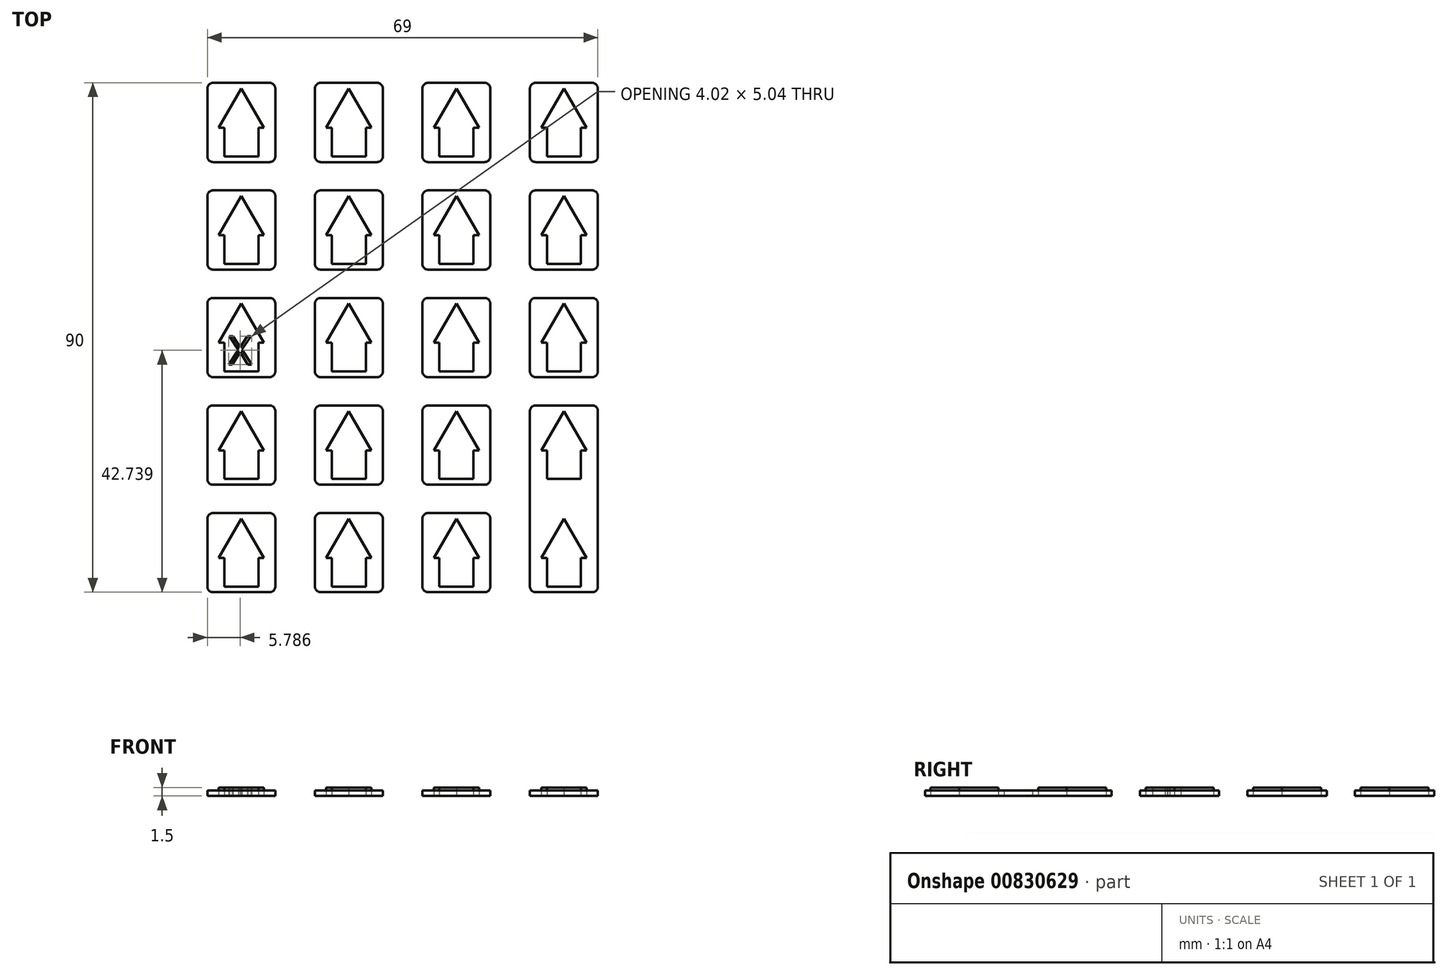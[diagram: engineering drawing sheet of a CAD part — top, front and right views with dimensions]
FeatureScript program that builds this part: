
annotation { "Feature Type Name" : "Feature", "Feature Type Description" : "" }
export const myFeature = defineFeature(function(context is Context, id is Id, definition is map)
    precondition{}
    {
        {
            var Q0;
            Q0=qCreatedBy(makeId("Top.planeOp"),FACE);
            var sketch = newSketch(context, id + "F0", { "sketchPlane" : qUnion([Q0])});
            skLineSegment(sketch, "E0.bottom", {"start": v(5, -7) * mm, "end": v(-5, -7) * mm});
            skLineSegment(sketch, "E0.top", {"start": v(5, 7) * mm, "end": v(-5, 7) * mm});
            skLineSegment(sketch, "E0.left", {"start": v(6, -6) * mm, "end": v(6, 6) * mm});
            skLineSegment(sketch, "E0.right", {"start": v(-6, -6) * mm, "end": v(-6, 6) * mm});
            skPoint(sketch, "E0.middle", {"position": v(0, 0) * mm});
            skPoint(sketch, "E1.visualSharp", {"position": v(-6, 7) * mm});
            skArc(sketch, "E1.filletArc", {"start": v(-5, 7) * mm, "mid": v(-5.7, 6.7) * mm, "end": v(-6, 6) * mm});
            skPoint(sketch, "E2.visualSharp", {"position": v(6, 7) * mm});
            skArc(sketch, "E2.filletArc", {"start": v(6, 6) * mm, "mid": v(5.7, 6.7) * mm, "end": v(5, 7) * mm});
            skPoint(sketch, "E3.visualSharp", {"position": v(6, -7) * mm});
            skArc(sketch, "E3.filletArc", {"start": v(5, -7) * mm, "mid": v(5.7, -6.7) * mm, "end": v(6, -6) * mm});
            skPoint(sketch, "E4.visualSharp", {"position": v(-6, -7) * mm});
            skArc(sketch, "E4.filletArc", {"start": v(-6, -6) * mm, "mid": v(-5.7, -6.7) * mm, "end": v(-5, -7) * mm});
            skLineSegment(sketch, "E5.0.1.0", {"start": v(6, 13) * mm, "end": v(6, 25) * mm});
            skLineSegment(sketch, "E5.0.1.1", {"start": v(-6, 13) * mm, "end": v(-6, 25) * mm});
            skLineSegment(sketch, "E5.0.1.2", {"start": v(5, 12) * mm, "end": v(-5, 12) * mm});
            skPoint(sketch, "E5.0.1.3", {"position": v(-6, 12) * mm});
            skPoint(sketch, "E5.0.1.4", {"position": v(0, 19) * mm});
            skPoint(sketch, "E5.0.1.5", {"position": v(-6, 26) * mm});
            skPoint(sketch, "E5.0.1.6", {"position": v(6, 26) * mm});
            skPoint(sketch, "E5.0.1.7", {"position": v(6, 12) * mm});
            skLineSegment(sketch, "E5.0.1.8", {"start": v(5, 26) * mm, "end": v(-5, 26) * mm});
            skArc(sketch, "E5.0.1.9", {"start": v(5, 12) * mm, "mid": v(5.7, 12.3) * mm, "end": v(6, 13) * mm});
            skArc(sketch, "E5.0.1.10", {"start": v(-6, 13) * mm, "mid": v(-5.7, 12.3) * mm, "end": v(-5, 12) * mm});
            skArc(sketch, "E5.0.1.11", {"start": v(6, 25) * mm, "mid": v(5.7, 25.7) * mm, "end": v(5, 26) * mm});
            skArc(sketch, "E5.0.1.12", {"start": v(-5, 26) * mm, "mid": v(-5.7, 25.7) * mm, "end": v(-6, 25) * mm});
            skLineSegment(sketch, "E5.0.2.0", {"start": v(6, 32) * mm, "end": v(6, 44) * mm});
            skLineSegment(sketch, "E5.0.2.1", {"start": v(-6, 32) * mm, "end": v(-6, 44) * mm});
            skLineSegment(sketch, "E5.0.2.2", {"start": v(5, 31) * mm, "end": v(-5, 31) * mm});
            skPoint(sketch, "E5.0.2.3", {"position": v(-6, 31) * mm});
            skPoint(sketch, "E5.0.2.4", {"position": v(0, 38) * mm});
            skPoint(sketch, "E5.0.2.5", {"position": v(-6, 45) * mm});
            skPoint(sketch, "E5.0.2.6", {"position": v(6, 45) * mm});
            skPoint(sketch, "E5.0.2.7", {"position": v(6, 31) * mm});
            skLineSegment(sketch, "E5.0.2.8", {"start": v(5, 45) * mm, "end": v(-5, 45) * mm});
            skArc(sketch, "E5.0.2.9", {"start": v(5, 31) * mm, "mid": v(5.7, 31.3) * mm, "end": v(6, 32) * mm});
            skArc(sketch, "E5.0.2.10", {"start": v(-6, 32) * mm, "mid": v(-5.7, 31.3) * mm, "end": v(-5, 31) * mm});
            skArc(sketch, "E5.0.2.11", {"start": v(6, 44) * mm, "mid": v(5.7, 44.7) * mm, "end": v(5, 45) * mm});
            skArc(sketch, "E5.0.2.12", {"start": v(-5, 45) * mm, "mid": v(-5.7, 44.7) * mm, "end": v(-6, 44) * mm});
            skLineSegment(sketch, "E5.0.3.0", {"start": v(6, 51) * mm, "end": v(6, 63) * mm});
            skLineSegment(sketch, "E5.0.3.1", {"start": v(-6, 51) * mm, "end": v(-6, 63) * mm});
            skLineSegment(sketch, "E5.0.3.2", {"start": v(5, 50) * mm, "end": v(-5, 50) * mm});
            skPoint(sketch, "E5.0.3.3", {"position": v(-6, 50) * mm});
            skPoint(sketch, "E5.0.3.4", {"position": v(0, 57) * mm});
            skPoint(sketch, "E5.0.3.5", {"position": v(-6, 64) * mm});
            skPoint(sketch, "E5.0.3.6", {"position": v(6, 64) * mm});
            skPoint(sketch, "E5.0.3.7", {"position": v(6, 50) * mm});
            skLineSegment(sketch, "E5.0.3.8", {"start": v(5, 64) * mm, "end": v(-5, 64) * mm});
            skArc(sketch, "E5.0.3.9", {"start": v(5, 50) * mm, "mid": v(5.7, 50.3) * mm, "end": v(6, 51) * mm});
            skArc(sketch, "E5.0.3.10", {"start": v(-6, 51) * mm, "mid": v(-5.7, 50.3) * mm, "end": v(-5, 50) * mm});
            skArc(sketch, "E5.0.3.11", {"start": v(6, 63) * mm, "mid": v(5.7, 63.7) * mm, "end": v(5, 64) * mm});
            skArc(sketch, "E5.0.3.12", {"start": v(-5, 64) * mm, "mid": v(-5.7, 63.7) * mm, "end": v(-6, 63) * mm});
            skLineSegment(sketch, "E5.0.4.0", {"start": v(6, 70) * mm, "end": v(6, 82) * mm});
            skLineSegment(sketch, "E5.0.4.1", {"start": v(-6, 70) * mm, "end": v(-6, 82) * mm});
            skLineSegment(sketch, "E5.0.4.2", {"start": v(5, 69) * mm, "end": v(-5, 69) * mm});
            skPoint(sketch, "E5.0.4.3", {"position": v(-6, 69) * mm});
            skPoint(sketch, "E5.0.4.4", {"position": v(0, 76) * mm});
            skPoint(sketch, "E5.0.4.5", {"position": v(-6, 83) * mm});
            skPoint(sketch, "E5.0.4.6", {"position": v(6, 83) * mm});
            skPoint(sketch, "E5.0.4.7", {"position": v(6, 69) * mm});
            skLineSegment(sketch, "E5.0.4.8", {"start": v(5, 83) * mm, "end": v(-5, 83) * mm});
            skArc(sketch, "E5.0.4.9", {"start": v(5, 69) * mm, "mid": v(5.7, 69.3) * mm, "end": v(6, 70) * mm});
            skArc(sketch, "E5.0.4.10", {"start": v(-6, 70) * mm, "mid": v(-5.7, 69.3) * mm, "end": v(-5, 69) * mm});
            skArc(sketch, "E5.0.4.11", {"start": v(6, 82) * mm, "mid": v(5.7, 82.7) * mm, "end": v(5, 83) * mm});
            skArc(sketch, "E5.0.4.12", {"start": v(-5, 83) * mm, "mid": v(-5.7, 82.7) * mm, "end": v(-6, 82) * mm});
            skLineSegment(sketch, "E5.1.0.0", {"start": v(25, -6) * mm, "end": v(25, 6) * mm});
            skLineSegment(sketch, "E5.1.0.1", {"start": v(13, -6) * mm, "end": v(13, 6) * mm});
            skLineSegment(sketch, "E5.1.0.2", {"start": v(24, -7) * mm, "end": v(14, -7) * mm});
            skPoint(sketch, "E5.1.0.3", {"position": v(13, -7) * mm});
            skPoint(sketch, "E5.1.0.4", {"position": v(19, 0) * mm});
            skPoint(sketch, "E5.1.0.5", {"position": v(13, 7) * mm});
            skPoint(sketch, "E5.1.0.6", {"position": v(25, 7) * mm});
            skPoint(sketch, "E5.1.0.7", {"position": v(25, -7) * mm});
            skLineSegment(sketch, "E5.1.0.8", {"start": v(24, 7) * mm, "end": v(14, 7) * mm});
            skArc(sketch, "E5.1.0.9", {"start": v(24, -7) * mm, "mid": v(24.7, -6.7) * mm, "end": v(25, -6) * mm});
            skArc(sketch, "E5.1.0.10", {"start": v(13, -6) * mm, "mid": v(13.3, -6.7) * mm, "end": v(14, -7) * mm});
            skArc(sketch, "E5.1.0.11", {"start": v(25, 6) * mm, "mid": v(24.7, 6.7) * mm, "end": v(24, 7) * mm});
            skArc(sketch, "E5.1.0.12", {"start": v(14, 7) * mm, "mid": v(13.3, 6.7) * mm, "end": v(13, 6) * mm});
            skLineSegment(sketch, "E5.1.1.0", {"start": v(25, 13) * mm, "end": v(25, 25) * mm});
            skLineSegment(sketch, "E5.1.1.1", {"start": v(13, 13) * mm, "end": v(13, 25) * mm});
            skLineSegment(sketch, "E5.1.1.2", {"start": v(24, 12) * mm, "end": v(14, 12) * mm});
            skPoint(sketch, "E5.1.1.3", {"position": v(13, 12) * mm});
            skPoint(sketch, "E5.1.1.4", {"position": v(19, 19) * mm});
            skPoint(sketch, "E5.1.1.5", {"position": v(13, 26) * mm});
            skPoint(sketch, "E5.1.1.6", {"position": v(25, 26) * mm});
            skPoint(sketch, "E5.1.1.7", {"position": v(25, 12) * mm});
            skLineSegment(sketch, "E5.1.1.8", {"start": v(24, 26) * mm, "end": v(14, 26) * mm});
            skArc(sketch, "E5.1.1.9", {"start": v(24, 12) * mm, "mid": v(24.7, 12.3) * mm, "end": v(25, 13) * mm});
            skArc(sketch, "E5.1.1.10", {"start": v(13, 13) * mm, "mid": v(13.3, 12.3) * mm, "end": v(14, 12) * mm});
            skArc(sketch, "E5.1.1.11", {"start": v(25, 25) * mm, "mid": v(24.7, 25.7) * mm, "end": v(24, 26) * mm});
            skArc(sketch, "E5.1.1.12", {"start": v(14, 26) * mm, "mid": v(13.3, 25.7) * mm, "end": v(13, 25) * mm});
            skLineSegment(sketch, "E5.1.2.0", {"start": v(25, 32) * mm, "end": v(25, 44) * mm});
            skLineSegment(sketch, "E5.1.2.1", {"start": v(13, 32) * mm, "end": v(13, 44) * mm});
            skLineSegment(sketch, "E5.1.2.2", {"start": v(24, 31) * mm, "end": v(14, 31) * mm});
            skPoint(sketch, "E5.1.2.3", {"position": v(13, 31) * mm});
            skPoint(sketch, "E5.1.2.4", {"position": v(19, 38) * mm});
            skPoint(sketch, "E5.1.2.5", {"position": v(13, 45) * mm});
            skPoint(sketch, "E5.1.2.6", {"position": v(25, 45) * mm});
            skPoint(sketch, "E5.1.2.7", {"position": v(25, 31) * mm});
            skLineSegment(sketch, "E5.1.2.8", {"start": v(24, 45) * mm, "end": v(14, 45) * mm});
            skArc(sketch, "E5.1.2.9", {"start": v(24, 31) * mm, "mid": v(24.7, 31.3) * mm, "end": v(25, 32) * mm});
            skArc(sketch, "E5.1.2.10", {"start": v(13, 32) * mm, "mid": v(13.3, 31.3) * mm, "end": v(14, 31) * mm});
            skArc(sketch, "E5.1.2.11", {"start": v(25, 44) * mm, "mid": v(24.7, 44.7) * mm, "end": v(24, 45) * mm});
            skArc(sketch, "E5.1.2.12", {"start": v(14, 45) * mm, "mid": v(13.3, 44.7) * mm, "end": v(13, 44) * mm});
            skLineSegment(sketch, "E5.1.3.0", {"start": v(25, 51) * mm, "end": v(25, 63) * mm});
            skLineSegment(sketch, "E5.1.3.1", {"start": v(13, 51) * mm, "end": v(13, 63) * mm});
            skLineSegment(sketch, "E5.1.3.2", {"start": v(24, 50) * mm, "end": v(14, 50) * mm});
            skPoint(sketch, "E5.1.3.3", {"position": v(13, 50) * mm});
            skPoint(sketch, "E5.1.3.4", {"position": v(19, 57) * mm});
            skPoint(sketch, "E5.1.3.5", {"position": v(13, 64) * mm});
            skPoint(sketch, "E5.1.3.6", {"position": v(25, 64) * mm});
            skPoint(sketch, "E5.1.3.7", {"position": v(25, 50) * mm});
            skLineSegment(sketch, "E5.1.3.8", {"start": v(24, 64) * mm, "end": v(14, 64) * mm});
            skArc(sketch, "E5.1.3.9", {"start": v(24, 50) * mm, "mid": v(24.7, 50.3) * mm, "end": v(25, 51) * mm});
            skArc(sketch, "E5.1.3.10", {"start": v(13, 51) * mm, "mid": v(13.3, 50.3) * mm, "end": v(14, 50) * mm});
            skArc(sketch, "E5.1.3.11", {"start": v(25, 63) * mm, "mid": v(24.7, 63.7) * mm, "end": v(24, 64) * mm});
            skArc(sketch, "E5.1.3.12", {"start": v(14, 64) * mm, "mid": v(13.3, 63.7) * mm, "end": v(13, 63) * mm});
            skLineSegment(sketch, "E5.1.4.0", {"start": v(25, 70) * mm, "end": v(25, 82) * mm});
            skLineSegment(sketch, "E5.1.4.1", {"start": v(13, 70) * mm, "end": v(13, 82) * mm});
            skLineSegment(sketch, "E5.1.4.2", {"start": v(24, 69) * mm, "end": v(14, 69) * mm});
            skPoint(sketch, "E5.1.4.3", {"position": v(13, 69) * mm});
            skPoint(sketch, "E5.1.4.4", {"position": v(19, 76) * mm});
            skPoint(sketch, "E5.1.4.5", {"position": v(13, 83) * mm});
            skPoint(sketch, "E5.1.4.6", {"position": v(25, 83) * mm});
            skPoint(sketch, "E5.1.4.7", {"position": v(25, 69) * mm});
            skLineSegment(sketch, "E5.1.4.8", {"start": v(24, 83) * mm, "end": v(14, 83) * mm});
            skArc(sketch, "E5.1.4.9", {"start": v(24, 69) * mm, "mid": v(24.7, 69.3) * mm, "end": v(25, 70) * mm});
            skArc(sketch, "E5.1.4.10", {"start": v(13, 70) * mm, "mid": v(13.3, 69.3) * mm, "end": v(14, 69) * mm});
            skArc(sketch, "E5.1.4.11", {"start": v(25, 82) * mm, "mid": v(24.7, 82.7) * mm, "end": v(24, 83) * mm});
            skArc(sketch, "E5.1.4.12", {"start": v(14, 83) * mm, "mid": v(13.3, 82.7) * mm, "end": v(13, 82) * mm});
            skLineSegment(sketch, "E5.2.0.0", {"start": v(44, -6) * mm, "end": v(44, 6) * mm});
            skLineSegment(sketch, "E5.2.0.1", {"start": v(32, -6) * mm, "end": v(32, 6) * mm});
            skLineSegment(sketch, "E5.2.0.2", {"start": v(43, -7) * mm, "end": v(33, -7) * mm});
            skPoint(sketch, "E5.2.0.3", {"position": v(32, -7) * mm});
            skPoint(sketch, "E5.2.0.4", {"position": v(38, 0) * mm});
            skPoint(sketch, "E5.2.0.5", {"position": v(32, 7) * mm});
            skPoint(sketch, "E5.2.0.6", {"position": v(44, 7) * mm});
            skPoint(sketch, "E5.2.0.7", {"position": v(44, -7) * mm});
            skLineSegment(sketch, "E5.2.0.8", {"start": v(43, 7) * mm, "end": v(33, 7) * mm});
            skArc(sketch, "E5.2.0.9", {"start": v(43, -7) * mm, "mid": v(43.7, -6.7) * mm, "end": v(44, -6) * mm});
            skArc(sketch, "E5.2.0.10", {"start": v(32, -6) * mm, "mid": v(32.3, -6.7) * mm, "end": v(33, -7) * mm});
            skArc(sketch, "E5.2.0.11", {"start": v(44, 6) * mm, "mid": v(43.7, 6.7) * mm, "end": v(43, 7) * mm});
            skArc(sketch, "E5.2.0.12", {"start": v(33, 7) * mm, "mid": v(32.3, 6.7) * mm, "end": v(32, 6) * mm});
            skLineSegment(sketch, "E5.2.1.0", {"start": v(44, 13) * mm, "end": v(44, 25) * mm});
            skLineSegment(sketch, "E5.2.1.1", {"start": v(32, 13) * mm, "end": v(32, 25) * mm});
            skLineSegment(sketch, "E5.2.1.2", {"start": v(43, 12) * mm, "end": v(33, 12) * mm});
            skPoint(sketch, "E5.2.1.3", {"position": v(32, 12) * mm});
            skPoint(sketch, "E5.2.1.4", {"position": v(38, 19) * mm});
            skPoint(sketch, "E5.2.1.5", {"position": v(32, 26) * mm});
            skPoint(sketch, "E5.2.1.6", {"position": v(44, 26) * mm});
            skPoint(sketch, "E5.2.1.7", {"position": v(44, 12) * mm});
            skLineSegment(sketch, "E5.2.1.8", {"start": v(43, 26) * mm, "end": v(33, 26) * mm});
            skArc(sketch, "E5.2.1.9", {"start": v(43, 12) * mm, "mid": v(43.7, 12.3) * mm, "end": v(44, 13) * mm});
            skArc(sketch, "E5.2.1.10", {"start": v(32, 13) * mm, "mid": v(32.3, 12.3) * mm, "end": v(33, 12) * mm});
            skArc(sketch, "E5.2.1.11", {"start": v(44, 25) * mm, "mid": v(43.7, 25.7) * mm, "end": v(43, 26) * mm});
            skArc(sketch, "E5.2.1.12", {"start": v(33, 26) * mm, "mid": v(32.3, 25.7) * mm, "end": v(32, 25) * mm});
            skLineSegment(sketch, "E5.2.2.0", {"start": v(44, 32) * mm, "end": v(44, 44) * mm});
            skLineSegment(sketch, "E5.2.2.1", {"start": v(32, 32) * mm, "end": v(32, 44) * mm});
            skLineSegment(sketch, "E5.2.2.2", {"start": v(43, 31) * mm, "end": v(33, 31) * mm});
            skPoint(sketch, "E5.2.2.3", {"position": v(32, 31) * mm});
            skPoint(sketch, "E5.2.2.4", {"position": v(38, 38) * mm});
            skPoint(sketch, "E5.2.2.5", {"position": v(32, 45) * mm});
            skPoint(sketch, "E5.2.2.6", {"position": v(44, 45) * mm});
            skPoint(sketch, "E5.2.2.7", {"position": v(44, 31) * mm});
            skLineSegment(sketch, "E5.2.2.8", {"start": v(43, 45) * mm, "end": v(33, 45) * mm});
            skArc(sketch, "E5.2.2.9", {"start": v(43, 31) * mm, "mid": v(43.7, 31.3) * mm, "end": v(44, 32) * mm});
            skArc(sketch, "E5.2.2.10", {"start": v(32, 32) * mm, "mid": v(32.3, 31.3) * mm, "end": v(33, 31) * mm});
            skArc(sketch, "E5.2.2.11", {"start": v(44, 44) * mm, "mid": v(43.7, 44.7) * mm, "end": v(43, 45) * mm});
            skArc(sketch, "E5.2.2.12", {"start": v(33, 45) * mm, "mid": v(32.3, 44.7) * mm, "end": v(32, 44) * mm});
            skLineSegment(sketch, "E5.2.3.0", {"start": v(44, 51) * mm, "end": v(44, 63) * mm});
            skLineSegment(sketch, "E5.2.3.1", {"start": v(32, 51) * mm, "end": v(32, 63) * mm});
            skLineSegment(sketch, "E5.2.3.2", {"start": v(43, 50) * mm, "end": v(33, 50) * mm});
            skPoint(sketch, "E5.2.3.3", {"position": v(32, 50) * mm});
            skPoint(sketch, "E5.2.3.4", {"position": v(38, 57) * mm});
            skPoint(sketch, "E5.2.3.5", {"position": v(32, 64) * mm});
            skPoint(sketch, "E5.2.3.6", {"position": v(44, 64) * mm});
            skPoint(sketch, "E5.2.3.7", {"position": v(44, 50) * mm});
            skLineSegment(sketch, "E5.2.3.8", {"start": v(43, 64) * mm, "end": v(33, 64) * mm});
            skArc(sketch, "E5.2.3.9", {"start": v(43, 50) * mm, "mid": v(43.7, 50.3) * mm, "end": v(44, 51) * mm});
            skArc(sketch, "E5.2.3.10", {"start": v(32, 51) * mm, "mid": v(32.3, 50.3) * mm, "end": v(33, 50) * mm});
            skArc(sketch, "E5.2.3.11", {"start": v(44, 63) * mm, "mid": v(43.7, 63.7) * mm, "end": v(43, 64) * mm});
            skArc(sketch, "E5.2.3.12", {"start": v(33, 64) * mm, "mid": v(32.3, 63.7) * mm, "end": v(32, 63) * mm});
            skLineSegment(sketch, "E5.2.4.0", {"start": v(44, 70) * mm, "end": v(44, 82) * mm});
            skLineSegment(sketch, "E5.2.4.1", {"start": v(32, 70) * mm, "end": v(32, 82) * mm});
            skLineSegment(sketch, "E5.2.4.2", {"start": v(43, 69) * mm, "end": v(33, 69) * mm});
            skPoint(sketch, "E5.2.4.3", {"position": v(32, 69) * mm});
            skPoint(sketch, "E5.2.4.4", {"position": v(38, 76) * mm});
            skPoint(sketch, "E5.2.4.5", {"position": v(32, 83) * mm});
            skPoint(sketch, "E5.2.4.6", {"position": v(44, 83) * mm});
            skPoint(sketch, "E5.2.4.7", {"position": v(44, 69) * mm});
            skLineSegment(sketch, "E5.2.4.8", {"start": v(43, 83) * mm, "end": v(33, 83) * mm});
            skArc(sketch, "E5.2.4.9", {"start": v(43, 69) * mm, "mid": v(43.7, 69.3) * mm, "end": v(44, 70) * mm});
            skArc(sketch, "E5.2.4.10", {"start": v(32, 70) * mm, "mid": v(32.3, 69.3) * mm, "end": v(33, 69) * mm});
            skArc(sketch, "E5.2.4.11", {"start": v(44, 82) * mm, "mid": v(43.7, 82.7) * mm, "end": v(43, 83) * mm});
            skArc(sketch, "E5.2.4.12", {"start": v(33, 83) * mm, "mid": v(32.3, 82.7) * mm, "end": v(32, 82) * mm});
            skLineSegment(sketch, "E5.3.0.2", {"start": v(62, -7) * mm, "end": v(52, -7) * mm});
            skPoint(sketch, "E5.3.0.3", {"position": v(51, -7) * mm});
            skPoint(sketch, "E5.3.0.4", {"position": v(57, 0) * mm});
            skPoint(sketch, "E5.3.0.7", {"position": v(63, -7) * mm});
            skArc(sketch, "E5.3.0.9", {"start": v(62, -7) * mm, "mid": v(62.7, -6.7) * mm, "end": v(63, -6) * mm});
            skArc(sketch, "E5.3.0.10", {"start": v(51, -6) * mm, "mid": v(51.3, -6.7) * mm, "end": v(52, -7) * mm});
            skLineSegment(sketch, "E5.3.1.0", {"start": v(63, -6) * mm, "end": v(63, 25) * mm});
            skLineSegment(sketch, "E5.3.1.1", {"start": v(51, -6) * mm, "end": v(51, 25) * mm});
            skPoint(sketch, "E5.3.1.4", {"position": v(57, 19) * mm});
            skPoint(sketch, "E5.3.1.5", {"position": v(51, 26) * mm});
            skPoint(sketch, "E5.3.1.6", {"position": v(63, 26) * mm});
            skLineSegment(sketch, "E5.3.1.8", {"start": v(62, 26) * mm, "end": v(52, 26) * mm});
            skArc(sketch, "E5.3.1.11", {"start": v(63, 25) * mm, "mid": v(62.7, 25.7) * mm, "end": v(62, 26) * mm});
            skArc(sketch, "E5.3.1.12", {"start": v(52, 26) * mm, "mid": v(51.3, 25.7) * mm, "end": v(51, 25) * mm});
            skLineSegment(sketch, "E5.3.2.0", {"start": v(63, 32) * mm, "end": v(63, 44) * mm});
            skLineSegment(sketch, "E5.3.2.1", {"start": v(51, 32) * mm, "end": v(51, 44) * mm});
            skLineSegment(sketch, "E5.3.2.2", {"start": v(62, 31) * mm, "end": v(52, 31) * mm});
            skPoint(sketch, "E5.3.2.3", {"position": v(51, 31) * mm});
            skPoint(sketch, "E5.3.2.4", {"position": v(57, 38) * mm});
            skPoint(sketch, "E5.3.2.5", {"position": v(51, 45) * mm});
            skPoint(sketch, "E5.3.2.6", {"position": v(63, 45) * mm});
            skPoint(sketch, "E5.3.2.7", {"position": v(63, 31) * mm});
            skLineSegment(sketch, "E5.3.2.8", {"start": v(62, 45) * mm, "end": v(52, 45) * mm});
            skArc(sketch, "E5.3.2.9", {"start": v(62, 31) * mm, "mid": v(62.7, 31.3) * mm, "end": v(63, 32) * mm});
            skArc(sketch, "E5.3.2.10", {"start": v(51, 32) * mm, "mid": v(51.3, 31.3) * mm, "end": v(52, 31) * mm});
            skArc(sketch, "E5.3.2.11", {"start": v(63, 44) * mm, "mid": v(62.7, 44.7) * mm, "end": v(62, 45) * mm});
            skArc(sketch, "E5.3.2.12", {"start": v(52, 45) * mm, "mid": v(51.3, 44.7) * mm, "end": v(51, 44) * mm});
            skLineSegment(sketch, "E5.3.3.0", {"start": v(63, 51) * mm, "end": v(63, 63) * mm});
            skLineSegment(sketch, "E5.3.3.1", {"start": v(51, 51) * mm, "end": v(51, 63) * mm});
            skLineSegment(sketch, "E5.3.3.2", {"start": v(62, 50) * mm, "end": v(52, 50) * mm});
            skPoint(sketch, "E5.3.3.3", {"position": v(51, 50) * mm});
            skPoint(sketch, "E5.3.3.4", {"position": v(57, 57) * mm});
            skPoint(sketch, "E5.3.3.5", {"position": v(51, 64) * mm});
            skPoint(sketch, "E5.3.3.6", {"position": v(63, 64) * mm});
            skPoint(sketch, "E5.3.3.7", {"position": v(63, 50) * mm});
            skLineSegment(sketch, "E5.3.3.8", {"start": v(62, 64) * mm, "end": v(52, 64) * mm});
            skArc(sketch, "E5.3.3.9", {"start": v(62, 50) * mm, "mid": v(62.7, 50.3) * mm, "end": v(63, 51) * mm});
            skArc(sketch, "E5.3.3.10", {"start": v(51, 51) * mm, "mid": v(51.3, 50.3) * mm, "end": v(52, 50) * mm});
            skArc(sketch, "E5.3.3.11", {"start": v(63, 63) * mm, "mid": v(62.7, 63.7) * mm, "end": v(62, 64) * mm});
            skArc(sketch, "E5.3.3.12", {"start": v(52, 64) * mm, "mid": v(51.3, 63.7) * mm, "end": v(51, 63) * mm});
            skLineSegment(sketch, "E5.3.4.0", {"start": v(63, 70) * mm, "end": v(63, 82) * mm});
            skLineSegment(sketch, "E5.3.4.1", {"start": v(51, 70) * mm, "end": v(51, 82) * mm});
            skLineSegment(sketch, "E5.3.4.2", {"start": v(62, 69) * mm, "end": v(52, 69) * mm});
            skPoint(sketch, "E5.3.4.3", {"position": v(51, 69) * mm});
            skPoint(sketch, "E5.3.4.4", {"position": v(57, 76) * mm});
            skPoint(sketch, "E5.3.4.5", {"position": v(51, 83) * mm});
            skPoint(sketch, "E5.3.4.6", {"position": v(63, 83) * mm});
            skPoint(sketch, "E5.3.4.7", {"position": v(63, 69) * mm});
            skLineSegment(sketch, "E5.3.4.8", {"start": v(62, 83) * mm, "end": v(52, 83) * mm});
            skArc(sketch, "E5.3.4.9", {"start": v(62, 69) * mm, "mid": v(62.7, 69.3) * mm, "end": v(63, 70) * mm});
            skArc(sketch, "E5.3.4.10", {"start": v(51, 70) * mm, "mid": v(51.3, 69.3) * mm, "end": v(52, 69) * mm});
            skArc(sketch, "E5.3.4.11", {"start": v(63, 82) * mm, "mid": v(62.7, 82.7) * mm, "end": v(62, 83) * mm});
            skArc(sketch, "E5.3.4.12", {"start": v(52, 83) * mm, "mid": v(51.3, 82.7) * mm, "end": v(51, 82) * mm});
            skLineSegment(sketch, "E5.direction1", {"start": v(-6, -7) * mm, "end": v(13, -7) * mm, "construction": true});
            skLineSegment(sketch, "E5.direction2", {"start": v(-6, -7) * mm, "end": v(-6, 12) * mm, "construction": true});
            skSolve(sketch);
        }
        {
            var Q0;
            Q0 = qSketchRegion(id + "F0", true);
            extrude(context, id + "F1", {"entities" : qUnion([Q0]), "depth" : 1 * mm, "offsetDistance" : 25 * mm});
        }
        {
            var Q0;
            Q0=qCreatedBy(makeId("Top.planeOp"),FACE);
            var sketch = newSketch(context, id + "F2", { "sketchPlane" : qUnion([Q0])});
            skLineSegment(sketch, "E6.bottom", {"start": v(3, -0.93) * mm, "end": v(4, -0.93) * mm});
            skLineSegment(sketch, "E6.top", {"start": v(-3, -6) * mm, "end": v(3, -6) * mm});
            skLineSegment(sketch, "E6.left", {"start": v(-3, -0.93) * mm, "end": v(-3, -6) * mm});
            skLineSegment(sketch, "E6.right", {"start": v(3, -0.93) * mm, "end": v(3, -6) * mm});
            skLineSegment(sketch, "E7", {"start": v(-4, -0.93) * mm, "end": v(0, 6) * mm});
            skLineSegment(sketch, "E8", {"start": v(0, 6) * mm, "end": v(4, -0.93) * mm});
            skLineSegment(sketch, "E9", {"start": v(0, 6) * mm, "end": v(0, -6) * mm, "construction": true});
            skLineSegment(sketch, "E10.trimOffspring", {"start": v(-4, -0.93) * mm, "end": v(-3, -0.93) * mm});
            skText(sketch, "E11", { "text": "X", "fontName": "OpenSans-Regular.ttf"});
            skLineSegment(sketch, "E12", {"start": v(-3, -2.24) * mm, "end": v(3, -2.24) * mm, "construction": true});
            skLineSegment(sketch, "E13.0.1.0", {"start": v(-3, 16.76) * mm, "end": v(3, 16.76) * mm, "construction": true});
            skLineSegment(sketch, "E13.0.1.1", {"start": v(-4, 18.07) * mm, "end": v(0, 25) * mm});
            skLineSegment(sketch, "E13.0.1.2", {"start": v(-3, 13) * mm, "end": v(3, 13) * mm});
            skLineSegment(sketch, "E13.0.1.3", {"start": v(0, 25) * mm, "end": v(0, 13) * mm, "construction": true});
            skLineSegment(sketch, "E13.0.1.4", {"start": v(0, 25) * mm, "end": v(4, 18.07) * mm});
            skLineSegment(sketch, "E13.0.1.5", {"start": v(-3, 18.07) * mm, "end": v(-3, 13) * mm});
            skLineSegment(sketch, "E13.0.1.6", {"start": v(3, 18.07) * mm, "end": v(3, 13) * mm});
            skLineSegment(sketch, "E13.0.1.7", {"start": v(3, 18.07) * mm, "end": v(4, 18.07) * mm});
            skLineSegment(sketch, "E13.0.1.8", {"start": v(-4, 18.07) * mm, "end": v(-3, 18.07) * mm});
            skLineSegment(sketch, "E13.0.2.0", {"start": v(-3, 35.76) * mm, "end": v(3, 35.76) * mm, "construction": true});
            skLineSegment(sketch, "E13.0.2.1", {"start": v(-4, 37.07) * mm, "end": v(0, 44) * mm});
            skLineSegment(sketch, "E13.0.2.2", {"start": v(-3, 32) * mm, "end": v(3, 32) * mm});
            skLineSegment(sketch, "E13.0.2.3", {"start": v(0, 44) * mm, "end": v(0, 32) * mm, "construction": true});
            skLineSegment(sketch, "E13.0.2.4", {"start": v(0, 44) * mm, "end": v(4, 37.07) * mm});
            skLineSegment(sketch, "E13.0.2.5", {"start": v(-3, 37.07) * mm, "end": v(-3, 32) * mm});
            skLineSegment(sketch, "E13.0.2.6", {"start": v(3, 37.07) * mm, "end": v(3, 32) * mm});
            skLineSegment(sketch, "E13.0.2.7", {"start": v(3, 37.07) * mm, "end": v(4, 37.07) * mm});
            skLineSegment(sketch, "E13.0.2.8", {"start": v(-4, 37.07) * mm, "end": v(-3, 37.07) * mm});
            skLineSegment(sketch, "E13.0.3.0", {"start": v(-3, 54.76) * mm, "end": v(3, 54.76) * mm, "construction": true});
            skLineSegment(sketch, "E13.0.3.1", {"start": v(-4, 56.07) * mm, "end": v(0, 63) * mm});
            skLineSegment(sketch, "E13.0.3.2", {"start": v(-3, 51) * mm, "end": v(3, 51) * mm});
            skLineSegment(sketch, "E13.0.3.3", {"start": v(0, 63) * mm, "end": v(0, 51) * mm, "construction": true});
            skLineSegment(sketch, "E13.0.3.4", {"start": v(0, 63) * mm, "end": v(4, 56.07) * mm});
            skLineSegment(sketch, "E13.0.3.5", {"start": v(-3, 56.07) * mm, "end": v(-3, 51) * mm});
            skLineSegment(sketch, "E13.0.3.6", {"start": v(3, 56.07) * mm, "end": v(3, 51) * mm});
            skLineSegment(sketch, "E13.0.3.7", {"start": v(3, 56.07) * mm, "end": v(4, 56.07) * mm});
            skLineSegment(sketch, "E13.0.3.8", {"start": v(-4, 56.07) * mm, "end": v(-3, 56.07) * mm});
            skLineSegment(sketch, "E13.0.4.0", {"start": v(-3, 73.76) * mm, "end": v(3, 73.76) * mm, "construction": true});
            skLineSegment(sketch, "E13.0.4.1", {"start": v(-4, 75.07) * mm, "end": v(0, 82) * mm});
            skLineSegment(sketch, "E13.0.4.2", {"start": v(-3, 70) * mm, "end": v(3, 70) * mm});
            skLineSegment(sketch, "E13.0.4.3", {"start": v(0, 82) * mm, "end": v(0, 70) * mm, "construction": true});
            skLineSegment(sketch, "E13.0.4.4", {"start": v(0, 82) * mm, "end": v(4, 75.07) * mm});
            skLineSegment(sketch, "E13.0.4.5", {"start": v(-3, 75.07) * mm, "end": v(-3, 70) * mm});
            skLineSegment(sketch, "E13.0.4.6", {"start": v(3, 75.07) * mm, "end": v(3, 70) * mm});
            skLineSegment(sketch, "E13.0.4.7", {"start": v(3, 75.07) * mm, "end": v(4, 75.07) * mm});
            skLineSegment(sketch, "E13.0.4.8", {"start": v(-4, 75.07) * mm, "end": v(-3, 75.07) * mm});
            skLineSegment(sketch, "E13.1.0.0", {"start": v(16, -2.24) * mm, "end": v(22, -2.24) * mm, "construction": true});
            skLineSegment(sketch, "E13.1.0.1", {"start": v(15, -0.93) * mm, "end": v(19, 6) * mm});
            skLineSegment(sketch, "E13.1.0.2", {"start": v(16, -6) * mm, "end": v(22, -6) * mm});
            skLineSegment(sketch, "E13.1.0.3", {"start": v(19, 6) * mm, "end": v(19, -6) * mm, "construction": true});
            skLineSegment(sketch, "E13.1.0.4", {"start": v(19, 6) * mm, "end": v(23, -0.93) * mm});
            skLineSegment(sketch, "E13.1.0.5", {"start": v(16, -0.93) * mm, "end": v(16, -6) * mm});
            skLineSegment(sketch, "E13.1.0.6", {"start": v(22, -0.93) * mm, "end": v(22, -6) * mm});
            skLineSegment(sketch, "E13.1.0.7", {"start": v(22, -0.93) * mm, "end": v(23, -0.93) * mm});
            skLineSegment(sketch, "E13.1.0.8", {"start": v(15, -0.93) * mm, "end": v(16, -0.93) * mm});
            skLineSegment(sketch, "E13.1.1.0", {"start": v(16, 16.76) * mm, "end": v(22, 16.76) * mm, "construction": true});
            skLineSegment(sketch, "E13.1.1.1", {"start": v(15, 18.07) * mm, "end": v(19, 25) * mm});
            skLineSegment(sketch, "E13.1.1.2", {"start": v(16, 13) * mm, "end": v(22, 13) * mm});
            skLineSegment(sketch, "E13.1.1.3", {"start": v(19, 25) * mm, "end": v(19, 13) * mm, "construction": true});
            skLineSegment(sketch, "E13.1.1.4", {"start": v(19, 25) * mm, "end": v(23, 18.07) * mm});
            skLineSegment(sketch, "E13.1.1.5", {"start": v(16, 18.07) * mm, "end": v(16, 13) * mm});
            skLineSegment(sketch, "E13.1.1.6", {"start": v(22, 18.07) * mm, "end": v(22, 13) * mm});
            skLineSegment(sketch, "E13.1.1.7", {"start": v(22, 18.07) * mm, "end": v(23, 18.07) * mm});
            skLineSegment(sketch, "E13.1.1.8", {"start": v(15, 18.07) * mm, "end": v(16, 18.07) * mm});
            skLineSegment(sketch, "E13.1.2.0", {"start": v(16, 35.76) * mm, "end": v(22, 35.76) * mm, "construction": true});
            skLineSegment(sketch, "E13.1.2.1", {"start": v(15, 37.07) * mm, "end": v(19, 44) * mm});
            skLineSegment(sketch, "E13.1.2.2", {"start": v(16, 32) * mm, "end": v(22, 32) * mm});
            skLineSegment(sketch, "E13.1.2.3", {"start": v(19, 44) * mm, "end": v(19, 32) * mm, "construction": true});
            skLineSegment(sketch, "E13.1.2.4", {"start": v(19, 44) * mm, "end": v(23, 37.07) * mm});
            skLineSegment(sketch, "E13.1.2.5", {"start": v(16, 37.07) * mm, "end": v(16, 32) * mm});
            skLineSegment(sketch, "E13.1.2.6", {"start": v(22, 37.07) * mm, "end": v(22, 32) * mm});
            skLineSegment(sketch, "E13.1.2.7", {"start": v(22, 37.07) * mm, "end": v(23, 37.07) * mm});
            skLineSegment(sketch, "E13.1.2.8", {"start": v(15, 37.07) * mm, "end": v(16, 37.07) * mm});
            skLineSegment(sketch, "E13.1.3.0", {"start": v(16, 54.76) * mm, "end": v(22, 54.76) * mm, "construction": true});
            skLineSegment(sketch, "E13.1.3.1", {"start": v(15, 56.07) * mm, "end": v(19, 63) * mm});
            skLineSegment(sketch, "E13.1.3.2", {"start": v(16, 51) * mm, "end": v(22, 51) * mm});
            skLineSegment(sketch, "E13.1.3.3", {"start": v(19, 63) * mm, "end": v(19, 51) * mm, "construction": true});
            skLineSegment(sketch, "E13.1.3.4", {"start": v(19, 63) * mm, "end": v(23, 56.07) * mm});
            skLineSegment(sketch, "E13.1.3.5", {"start": v(16, 56.07) * mm, "end": v(16, 51) * mm});
            skLineSegment(sketch, "E13.1.3.6", {"start": v(22, 56.07) * mm, "end": v(22, 51) * mm});
            skLineSegment(sketch, "E13.1.3.7", {"start": v(22, 56.07) * mm, "end": v(23, 56.07) * mm});
            skLineSegment(sketch, "E13.1.3.8", {"start": v(15, 56.07) * mm, "end": v(16, 56.07) * mm});
            skLineSegment(sketch, "E13.1.4.0", {"start": v(16, 73.76) * mm, "end": v(22, 73.76) * mm, "construction": true});
            skLineSegment(sketch, "E13.1.4.1", {"start": v(15, 75.07) * mm, "end": v(19, 82) * mm});
            skLineSegment(sketch, "E13.1.4.2", {"start": v(16, 70) * mm, "end": v(22, 70) * mm});
            skLineSegment(sketch, "E13.1.4.3", {"start": v(19, 82) * mm, "end": v(19, 70) * mm, "construction": true});
            skLineSegment(sketch, "E13.1.4.4", {"start": v(19, 82) * mm, "end": v(23, 75.07) * mm});
            skLineSegment(sketch, "E13.1.4.5", {"start": v(16, 75.07) * mm, "end": v(16, 70) * mm});
            skLineSegment(sketch, "E13.1.4.6", {"start": v(22, 75.07) * mm, "end": v(22, 70) * mm});
            skLineSegment(sketch, "E13.1.4.7", {"start": v(22, 75.07) * mm, "end": v(23, 75.07) * mm});
            skLineSegment(sketch, "E13.1.4.8", {"start": v(15, 75.07) * mm, "end": v(16, 75.07) * mm});
            skLineSegment(sketch, "E13.2.0.0", {"start": v(35, -2.24) * mm, "end": v(41, -2.24) * mm, "construction": true});
            skLineSegment(sketch, "E13.2.0.1", {"start": v(34, -0.93) * mm, "end": v(38, 6) * mm});
            skLineSegment(sketch, "E13.2.0.2", {"start": v(35, -6) * mm, "end": v(41, -6) * mm});
            skLineSegment(sketch, "E13.2.0.3", {"start": v(38, 6) * mm, "end": v(38, -6) * mm, "construction": true});
            skLineSegment(sketch, "E13.2.0.4", {"start": v(38, 6) * mm, "end": v(42, -0.93) * mm});
            skLineSegment(sketch, "E13.2.0.5", {"start": v(35, -0.93) * mm, "end": v(35, -6) * mm});
            skLineSegment(sketch, "E13.2.0.6", {"start": v(41, -0.93) * mm, "end": v(41, -6) * mm});
            skLineSegment(sketch, "E13.2.0.7", {"start": v(41, -0.93) * mm, "end": v(42, -0.93) * mm});
            skLineSegment(sketch, "E13.2.0.8", {"start": v(34, -0.93) * mm, "end": v(35, -0.93) * mm});
            skLineSegment(sketch, "E13.2.1.0", {"start": v(35, 16.76) * mm, "end": v(41, 16.76) * mm, "construction": true});
            skLineSegment(sketch, "E13.2.1.1", {"start": v(34, 18.07) * mm, "end": v(38, 25) * mm});
            skLineSegment(sketch, "E13.2.1.2", {"start": v(35, 13) * mm, "end": v(41, 13) * mm});
            skLineSegment(sketch, "E13.2.1.3", {"start": v(38, 25) * mm, "end": v(38, 13) * mm, "construction": true});
            skLineSegment(sketch, "E13.2.1.4", {"start": v(38, 25) * mm, "end": v(42, 18.07) * mm});
            skLineSegment(sketch, "E13.2.1.5", {"start": v(35, 18.07) * mm, "end": v(35, 13) * mm});
            skLineSegment(sketch, "E13.2.1.6", {"start": v(41, 18.07) * mm, "end": v(41, 13) * mm});
            skLineSegment(sketch, "E13.2.1.7", {"start": v(41, 18.07) * mm, "end": v(42, 18.07) * mm});
            skLineSegment(sketch, "E13.2.1.8", {"start": v(34, 18.07) * mm, "end": v(35, 18.07) * mm});
            skLineSegment(sketch, "E13.2.2.0", {"start": v(35, 35.76) * mm, "end": v(41, 35.76) * mm, "construction": true});
            skLineSegment(sketch, "E13.2.2.1", {"start": v(34, 37.07) * mm, "end": v(38, 44) * mm});
            skLineSegment(sketch, "E13.2.2.2", {"start": v(35, 32) * mm, "end": v(41, 32) * mm});
            skLineSegment(sketch, "E13.2.2.3", {"start": v(38, 44) * mm, "end": v(38, 32) * mm, "construction": true});
            skLineSegment(sketch, "E13.2.2.4", {"start": v(38, 44) * mm, "end": v(42, 37.07) * mm});
            skLineSegment(sketch, "E13.2.2.5", {"start": v(35, 37.07) * mm, "end": v(35, 32) * mm});
            skLineSegment(sketch, "E13.2.2.6", {"start": v(41, 37.07) * mm, "end": v(41, 32) * mm});
            skLineSegment(sketch, "E13.2.2.7", {"start": v(41, 37.07) * mm, "end": v(42, 37.07) * mm});
            skLineSegment(sketch, "E13.2.2.8", {"start": v(34, 37.07) * mm, "end": v(35, 37.07) * mm});
            skLineSegment(sketch, "E13.2.3.0", {"start": v(35, 54.76) * mm, "end": v(41, 54.76) * mm, "construction": true});
            skLineSegment(sketch, "E13.2.3.1", {"start": v(34, 56.07) * mm, "end": v(38, 63) * mm});
            skLineSegment(sketch, "E13.2.3.2", {"start": v(35, 51) * mm, "end": v(41, 51) * mm});
            skLineSegment(sketch, "E13.2.3.3", {"start": v(38, 63) * mm, "end": v(38, 51) * mm, "construction": true});
            skLineSegment(sketch, "E13.2.3.4", {"start": v(38, 63) * mm, "end": v(42, 56.07) * mm});
            skLineSegment(sketch, "E13.2.3.5", {"start": v(35, 56.07) * mm, "end": v(35, 51) * mm});
            skLineSegment(sketch, "E13.2.3.6", {"start": v(41, 56.07) * mm, "end": v(41, 51) * mm});
            skLineSegment(sketch, "E13.2.3.7", {"start": v(41, 56.07) * mm, "end": v(42, 56.07) * mm});
            skLineSegment(sketch, "E13.2.3.8", {"start": v(34, 56.07) * mm, "end": v(35, 56.07) * mm});
            skLineSegment(sketch, "E13.2.4.0", {"start": v(35, 73.76) * mm, "end": v(41, 73.76) * mm, "construction": true});
            skLineSegment(sketch, "E13.2.4.1", {"start": v(34, 75.07) * mm, "end": v(38, 82) * mm});
            skLineSegment(sketch, "E13.2.4.2", {"start": v(35, 70) * mm, "end": v(41, 70) * mm});
            skLineSegment(sketch, "E13.2.4.3", {"start": v(38, 82) * mm, "end": v(38, 70) * mm, "construction": true});
            skLineSegment(sketch, "E13.2.4.4", {"start": v(38, 82) * mm, "end": v(42, 75.07) * mm});
            skLineSegment(sketch, "E13.2.4.5", {"start": v(35, 75.07) * mm, "end": v(35, 70) * mm});
            skLineSegment(sketch, "E13.2.4.6", {"start": v(41, 75.07) * mm, "end": v(41, 70) * mm});
            skLineSegment(sketch, "E13.2.4.7", {"start": v(41, 75.07) * mm, "end": v(42, 75.07) * mm});
            skLineSegment(sketch, "E13.2.4.8", {"start": v(34, 75.07) * mm, "end": v(35, 75.07) * mm});
            skLineSegment(sketch, "E13.3.0.0", {"start": v(54, -2.24) * mm, "end": v(60, -2.24) * mm, "construction": true});
            skLineSegment(sketch, "E13.3.0.1", {"start": v(53, -0.93) * mm, "end": v(57, 6) * mm});
            skLineSegment(sketch, "E13.3.0.2", {"start": v(54, -6) * mm, "end": v(60, -6) * mm});
            skLineSegment(sketch, "E13.3.0.3", {"start": v(57, 6) * mm, "end": v(57, -6) * mm, "construction": true});
            skLineSegment(sketch, "E13.3.0.4", {"start": v(57, 6) * mm, "end": v(61, -0.93) * mm});
            skLineSegment(sketch, "E13.3.0.5", {"start": v(54, -0.93) * mm, "end": v(54, -6) * mm});
            skLineSegment(sketch, "E13.3.0.6", {"start": v(60, -0.93) * mm, "end": v(60, -6) * mm});
            skLineSegment(sketch, "E13.3.0.7", {"start": v(60, -0.93) * mm, "end": v(61, -0.93) * mm});
            skLineSegment(sketch, "E13.3.0.8", {"start": v(53, -0.93) * mm, "end": v(54, -0.93) * mm});
            skLineSegment(sketch, "E13.3.1.0", {"start": v(54, 16.76) * mm, "end": v(60, 16.76) * mm, "construction": true});
            skLineSegment(sketch, "E13.3.1.1", {"start": v(53, 18.07) * mm, "end": v(57, 25) * mm});
            skLineSegment(sketch, "E13.3.1.2", {"start": v(54, 13) * mm, "end": v(60, 13) * mm});
            skLineSegment(sketch, "E13.3.1.3", {"start": v(57, 25) * mm, "end": v(57, 13) * mm, "construction": true});
            skLineSegment(sketch, "E13.3.1.4", {"start": v(57, 25) * mm, "end": v(61, 18.07) * mm});
            skLineSegment(sketch, "E13.3.1.5", {"start": v(54, 18.07) * mm, "end": v(54, 13) * mm});
            skLineSegment(sketch, "E13.3.1.6", {"start": v(60, 18.07) * mm, "end": v(60, 13) * mm});
            skLineSegment(sketch, "E13.3.1.7", {"start": v(60, 18.07) * mm, "end": v(61, 18.07) * mm});
            skLineSegment(sketch, "E13.3.1.8", {"start": v(53, 18.07) * mm, "end": v(54, 18.07) * mm});
            skLineSegment(sketch, "E13.3.2.0", {"start": v(54, 35.76) * mm, "end": v(60, 35.76) * mm, "construction": true});
            skLineSegment(sketch, "E13.3.2.1", {"start": v(53, 37.07) * mm, "end": v(57, 44) * mm});
            skLineSegment(sketch, "E13.3.2.2", {"start": v(54, 32) * mm, "end": v(60, 32) * mm});
            skLineSegment(sketch, "E13.3.2.3", {"start": v(57, 44) * mm, "end": v(57, 32) * mm, "construction": true});
            skLineSegment(sketch, "E13.3.2.4", {"start": v(57, 44) * mm, "end": v(61, 37.07) * mm});
            skLineSegment(sketch, "E13.3.2.5", {"start": v(54, 37.07) * mm, "end": v(54, 32) * mm});
            skLineSegment(sketch, "E13.3.2.6", {"start": v(60, 37.07) * mm, "end": v(60, 32) * mm});
            skLineSegment(sketch, "E13.3.2.7", {"start": v(60, 37.07) * mm, "end": v(61, 37.07) * mm});
            skLineSegment(sketch, "E13.3.2.8", {"start": v(53, 37.07) * mm, "end": v(54, 37.07) * mm});
            skLineSegment(sketch, "E13.3.3.0", {"start": v(54, 54.76) * mm, "end": v(60, 54.76) * mm, "construction": true});
            skLineSegment(sketch, "E13.3.3.1", {"start": v(53, 56.07) * mm, "end": v(57, 63) * mm});
            skLineSegment(sketch, "E13.3.3.2", {"start": v(54, 51) * mm, "end": v(60, 51) * mm});
            skLineSegment(sketch, "E13.3.3.3", {"start": v(57, 63) * mm, "end": v(57, 51) * mm, "construction": true});
            skLineSegment(sketch, "E13.3.3.4", {"start": v(57, 63) * mm, "end": v(61, 56.07) * mm});
            skLineSegment(sketch, "E13.3.3.5", {"start": v(54, 56.07) * mm, "end": v(54, 51) * mm});
            skLineSegment(sketch, "E13.3.3.6", {"start": v(60, 56.07) * mm, "end": v(60, 51) * mm});
            skLineSegment(sketch, "E13.3.3.7", {"start": v(60, 56.07) * mm, "end": v(61, 56.07) * mm});
            skLineSegment(sketch, "E13.3.3.8", {"start": v(53, 56.07) * mm, "end": v(54, 56.07) * mm});
            skLineSegment(sketch, "E13.3.4.0", {"start": v(54, 73.76) * mm, "end": v(60, 73.76) * mm, "construction": true});
            skLineSegment(sketch, "E13.3.4.1", {"start": v(53, 75.07) * mm, "end": v(57, 82) * mm});
            skLineSegment(sketch, "E13.3.4.2", {"start": v(54, 70) * mm, "end": v(60, 70) * mm});
            skLineSegment(sketch, "E13.3.4.3", {"start": v(57, 82) * mm, "end": v(57, 70) * mm, "construction": true});
            skLineSegment(sketch, "E13.3.4.4", {"start": v(57, 82) * mm, "end": v(61, 75.07) * mm});
            skLineSegment(sketch, "E13.3.4.5", {"start": v(54, 75.07) * mm, "end": v(54, 70) * mm});
            skLineSegment(sketch, "E13.3.4.6", {"start": v(60, 75.07) * mm, "end": v(60, 70) * mm});
            skLineSegment(sketch, "E13.3.4.7", {"start": v(60, 75.07) * mm, "end": v(61, 75.07) * mm});
            skLineSegment(sketch, "E13.3.4.8", {"start": v(53, 75.07) * mm, "end": v(54, 75.07) * mm});
            skLineSegment(sketch, "E13.direction1", {"start": v(-3, -6) * mm, "end": v(16, -6) * mm, "construction": true});
            skLineSegment(sketch, "E13.direction2", {"start": v(-3, -6) * mm, "end": v(-3, 13) * mm, "construction": true});
            const initialGuessF2  = {"E11": [-0.00225, 0.03322, 1, 0, 0.00508]};
            skSetInitialGuess(sketch, initialGuessF2);
            skSolve(sketch);
        }
        {
            var Q0;
            Q0 = qSketchRegion(id + "F2", true);
            extrude(context, id + "F3", {"entities" : qUnion([Q0]), "depth" : 1.5 * mm, "offsetDistance" : 25 * mm});
        }
    });
